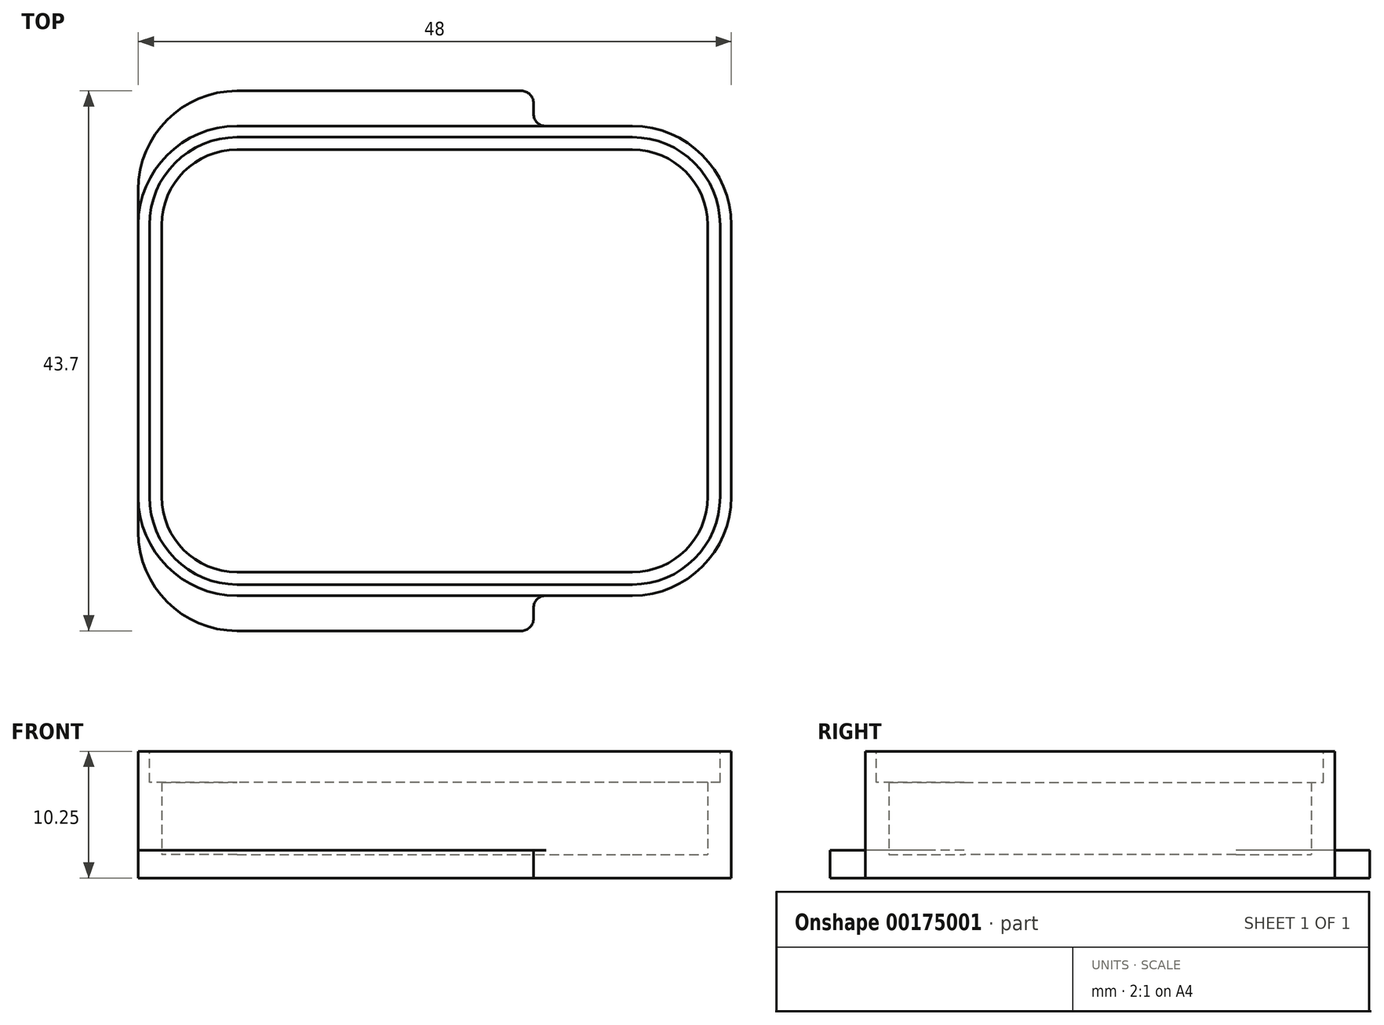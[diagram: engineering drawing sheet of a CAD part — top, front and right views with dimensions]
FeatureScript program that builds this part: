
annotation { "Feature Type Name" : "Feature", "Feature Type Description" : "" }
export const myFeature = defineFeature(function(context is Context, id is Id, definition is map)
    precondition{}
    {
        {
            var Q0;
            Q0=qCreatedBy(makeId("Top.planeOp"),FACE);
            var sketch = newSketch(context, id + "F0", { "sketchPlane" : qUnion([Q0])});
            skLineSegment(sketch, "E0.bottom", {"start": v(-16, 19) * mm, "end": v(16, 19) * mm});
            skLineSegment(sketch, "E0.top", {"start": v(-16, -19) * mm, "end": v(16, -19) * mm});
            skLineSegment(sketch, "E0.left", {"start": v(-24, 11) * mm, "end": v(-24, -11) * mm});
            skLineSegment(sketch, "E0.right", {"start": v(24, 11) * mm, "end": v(24, -11) * mm});
            skPoint(sketch, "E1.visualSharp", {"position": v(-24, 19) * mm});
            skArc(sketch, "E1.filletArc", {"start": v(-16, 19) * mm, "mid": v(-21.66, 16.66) * mm, "end": v(-24, 11) * mm});
            skArc(sketch, "E2.filletArc", {"start": v(24, 11) * mm, "mid": v(21.66, 16.66) * mm, "end": v(16, 19) * mm});
            skPoint(sketch, "E3.visualSharp", {"position": v(24, -19) * mm});
            skArc(sketch, "E3.filletArc", {"start": v(16, -19) * mm, "mid": v(21.66, -16.66) * mm, "end": v(24, -11) * mm});
            skPoint(sketch, "E4.visualSharp", {"position": v(-24, -19) * mm});
            skArc(sketch, "E4.filletArc", {"start": v(-24, -11) * mm, "mid": v(-21.66, -16.66) * mm, "end": v(-16, -19) * mm});
            skSolve(sketch);
        }
        {
            var Q0;
            Q0=makeQuery(id+"F0.imprint","IMPRINT",FACE,{"disambiguationData":[TD([[makeQuery(id+"F0.imprint","IMPRINT",EDGE,{"derivedFrom":sQuery(id+"F0.wireOp",EDGE,"E0.bottom")}),-1.0]])]});
            extrude(context, id + "F1", {"entities" : qUnion([Q0]), "depth" : 10.25 * mm});
        }
        {
            var Q0;
            Q0=qCreatedBy(makeId("Top.planeOp"),FACE);
            var sketch = newSketch(context, id + "F2", { "sketchPlane" : qUnion([Q0])});
            skLineSegment(sketch, "E5.bottom", {"start": v(-16, 21.85) * mm, "end": v(8, 21.85) * mm});
            skLineSegment(sketch, "E5.top", {"start": v(-16, -21.85) * mm, "end": v(8, -21.85) * mm});
            skLineSegment(sketch, "E5.left", {"start": v(-24, 13.85) * mm, "end": v(-24, -13.85) * mm});
            skLineSegment(sketch, "E5.right", {"start": v(8, 21.85) * mm, "end": v(8, -21.85) * mm});
            skPoint(sketch, "E6.visualSharp", {"position": v(-24, -21.85) * mm});
            skArc(sketch, "E6.filletArc", {"start": v(-24, -13.85) * mm, "mid": v(-21.66, -19.5) * mm, "end": v(-16, -21.85) * mm});
            skPoint(sketch, "E7.visualSharp", {"position": v(-24, 21.85) * mm});
            skArc(sketch, "E7.filletArc", {"start": v(-16, 21.85) * mm, "mid": v(-21.66, 19.5) * mm, "end": v(-24, 13.85) * mm});
            skSolve(sketch);
        }
        {
            var Q0;
            Q0=makeQuery(id+"F2.imprint","IMPRINT",FACE,{"disambiguationData":[TD([[makeQuery(id+"F2.imprint","IMPRINT",EDGE,{"derivedFrom":sQuery(id+"F2.wireOp",EDGE,"E5.bottom")}),-1.0]])]});
            extrude(context, id + "F3", {"entities" : qUnion([Q0]), "operationType" : NewBodyOperationType.ADD, "depth" : 2.25 * mm});
        }
        {
            var Q0;
            Q0=makeQuery(id+"F3.opExtrude","SWEPT_EDGE",EDGE,{"disambiguationData":[OSD([sQuery(id+"F2.wireOp",EDGE,"E5.bottom"),sQuery(id+"F2.wireOp",EDGE,"E5.right")])]});
            var Q1;
            Q1=makeQuery(id+"F3.boolean.opBoolean","INTERSECT",EDGE,{"derivedFrom":[makeQuery(id+"F1.opExtrude","SWEPT_FACE",FACE,{"disambiguationData":[OSD([sQuery(id+"F0.wireOp",EDGE,"E0.bottom")])]}),makeQuery(id+"F3.opExtrude","SWEPT_FACE",FACE,{"disambiguationData":[OSD([sQuery(id+"F2.wireOp",EDGE,"E5.right")])]})]});
            var Q2;
            Q2=makeQuery(id+"F3.boolean.opBoolean","INTERSECT",EDGE,{"derivedFrom":[makeQuery(id+"F1.opExtrude","SWEPT_FACE",FACE,{"disambiguationData":[OSD([sQuery(id+"F0.wireOp",EDGE,"E0.top")])]}),makeQuery(id+"F3.opExtrude","SWEPT_FACE",FACE,{"disambiguationData":[OSD([sQuery(id+"F2.wireOp",EDGE,"E5.right")])]})]});
            var Q3;
            Q3=makeQuery(id+"F3.opExtrude","SWEPT_EDGE",EDGE,{"disambiguationData":[OSD([sQuery(id+"F2.wireOp",EDGE,"E5.top"),sQuery(id+"F2.wireOp",EDGE,"E5.right")])]});
            fillet(context, id + "F4", {"entities" : qUnion([Q0, Q1, Q2, Q3]), "radius" : 1 * mm, "tangentPropagation" : true, "allowEdgeOverflow" : false});
        }
        {
            var Q0;
            Q0=makeQuery(id+"F1.opExtrude","CAP_FACE",FACE,{"disambiguationData":[OSD([sQuery(id+"F0.wireOp",EDGE,"E0.bottom"),sQuery(id+"F0.wireOp",EDGE,"E0.top"),sQuery(id+"F0.wireOp",EDGE,"E0.left"),sQuery(id+"F0.wireOp",EDGE,"E0.right"),sQuery(id+"F0.wireOp",EDGE,"E1.filletArc"),sQuery(id+"F0.wireOp",EDGE,"E2.filletArc"),sQuery(id+"F0.wireOp",EDGE,"E3.filletArc"),sQuery(id+"F0.wireOp",EDGE,"E4.filletArc")])],"isStart":false});
            shell(context, id + "F5", {"entities" : qUnion([Q0]), "thickness" : 1.9 * mm});
        }
        {
            var Q0;
            Q0=makeQuery(id+"F1.opExtrude","CAP_FACE",FACE,{"disambiguationData":[OSD([sQuery(id+"F0.wireOp",EDGE,"E0.bottom"),sQuery(id+"F0.wireOp",EDGE,"E0.top"),sQuery(id+"F0.wireOp",EDGE,"E0.left"),sQuery(id+"F0.wireOp",EDGE,"E0.right"),sQuery(id+"F0.wireOp",EDGE,"E1.filletArc"),sQuery(id+"F0.wireOp",EDGE,"E2.filletArc"),sQuery(id+"F0.wireOp",EDGE,"E3.filletArc"),sQuery(id+"F0.wireOp",EDGE,"E4.filletArc")])],"isStart":false});
            var sketch = newSketch(context, id + "F6", { "sketchPlane" : qUnion([Q0])});
            skArc(sketch, "E8.0", {"start": v(23.1, 11) * mm, "mid": v(21.02, 16.02) * mm, "end": v(16, 18.1) * mm});
            skLineSegment(sketch, "E8.1", {"start": v(23.1, -11) * mm, "end": v(23.1, 11) * mm});
            skLineSegment(sketch, "E8.2", {"start": v(16, 18.1) * mm, "end": v(-16, 18.1) * mm});
            skArc(sketch, "E8.3", {"start": v(16, -18.1) * mm, "mid": v(21.02, -16.02) * mm, "end": v(23.1, -11) * mm});
            skArc(sketch, "E8.4", {"start": v(-16, 18.1) * mm, "mid": v(-21.02, 16.02) * mm, "end": v(-23.1, 11) * mm});
            skLineSegment(sketch, "E8.5", {"start": v(-23.1, 11) * mm, "end": v(-23.1, -11) * mm});
            skArc(sketch, "E8.6", {"start": v(-23.1, -11) * mm, "mid": v(-21.02, -16.02) * mm, "end": v(-16, -18.1) * mm});
            skLineSegment(sketch, "E8.7", {"start": v(-16, -18.1) * mm, "end": v(16, -18.1) * mm});
            skSolve(sketch);
        }
        {
            var Q0;
            Q0=makeQuery(id+"F6.imprint","IMPRINT",FACE,{"disambiguationData":[TD([[makeQuery(id+"F6.imprint","IMPRINT",EDGE,{"derivedFrom":sQuery(id+"F6.wireOp",EDGE,"E8.0")}),1.0]])]});
            extrude(context, id + "F7", {"entities" : qUnion([Q0]), "operationType" : NewBodyOperationType.REMOVE, "oppositeDirection" : true, "depth" : 2.5 * mm});
        }
    });
